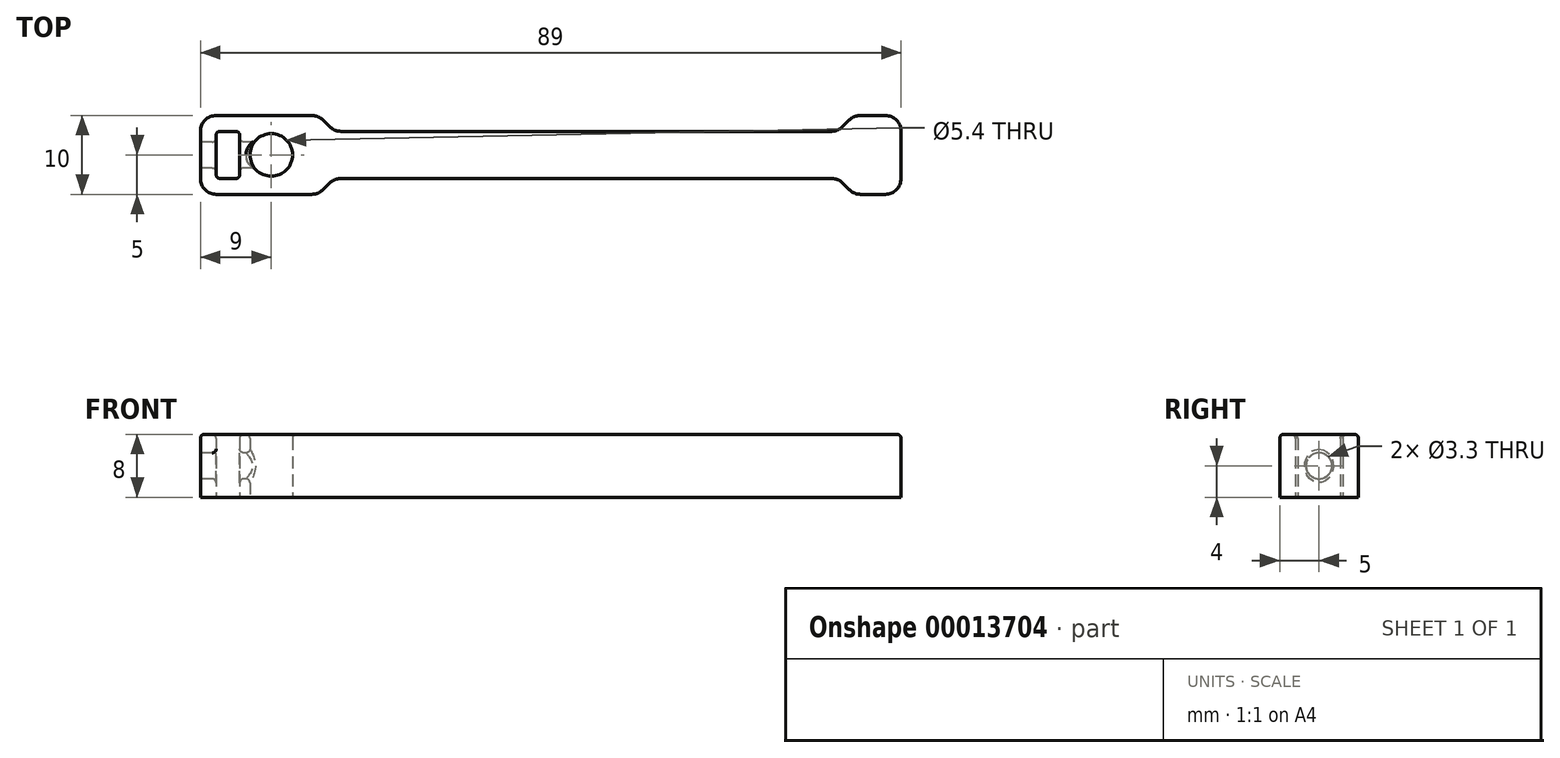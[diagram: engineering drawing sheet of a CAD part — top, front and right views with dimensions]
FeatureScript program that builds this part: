
annotation { "Feature Type Name" : "Feature", "Feature Type Description" : "" }
export const myFeature = defineFeature(function(context is Context, id is Id, definition is map)
    precondition{}
    {
        {
            var Q0;
            Q0=qCreatedBy(makeId("Top.planeOp"),FACE);
            var sketch = newSketch(context, id + "F0", { "sketchPlane" : qUnion([Q0])});
            skCircle(sketch, "E0", {"center": v(0, 0) * mm, "radius": 2.7 * mm});
            skLineSegment(sketch, "E1", {"start": v(0, 0) * mm, "end": v(80, 0) * mm, "construction": true});
            skLineSegment(sketch, "E2", {"start": v(-9, 5) * mm, "end": v(80, 5) * mm});
            skLineSegment(sketch, "E3", {"start": v(-9, -5) * mm, "end": v(80, -5) * mm});
            skLineSegment(sketch, "E4", {"start": v(80, -5) * mm, "end": v(80, 0) * mm});
            skLineSegment(sketch, "E5", {"start": v(80, 0) * mm, "end": v(80, 5) * mm});
            skLineSegment(sketch, "E6", {"start": v(-9, -5) * mm, "end": v(-9, 5) * mm});
            skLineSegment(sketch, "E7.rect.bottom", {"start": v(-4, 3) * mm, "end": v(-7, 3) * mm});
            skLineSegment(sketch, "E7.rect.top", {"start": v(-4, -3) * mm, "end": v(-7, -3) * mm});
            skLineSegment(sketch, "E7.rect.left", {"start": v(-4, 3) * mm, "end": v(-4, -3) * mm});
            skLineSegment(sketch, "E7.rect.right", {"start": v(-7, 3) * mm, "end": v(-7, -3) * mm});
            skPoint(sketch, "E7.rect.middle", {"position": v(-5.5, 0) * mm});
            skLineSegment(sketch, "E8", {"start": v(6, 5) * mm, "end": v(8, 3) * mm});
            skLineSegment(sketch, "E9", {"start": v(6, -5) * mm, "end": v(8, -3) * mm});
            skLineSegment(sketch, "E10", {"start": v(8, 3) * mm, "end": v(72, 3) * mm});
            skLineSegment(sketch, "E11", {"start": v(8, -3) * mm, "end": v(72, -3) * mm});
            skLineSegment(sketch, "E12", {"start": v(72, -3) * mm, "end": v(74, -5) * mm});
            skLineSegment(sketch, "E13", {"start": v(72, 3) * mm, "end": v(74, 5) * mm});
            skSolve(sketch);
        }
        {
            var Q0;
            Q0=makeQuery(id+"F0.imprint","IMPRINT",FACE,{"disambiguationData":[TD([[makeQuery(id+"F0.imprint","IMPRINT",EDGE,{"derivedFrom":sQuery(id+"F0.wireOp",EDGE,"E0")}),-1.0]])]});
            extrude(context, id + "F1", {"entities" : qUnion([Q0]), "depth" : 8 * mm});
        }
        {
            var Q0;
            Q0=makeQuery(id+"F1.opExtrude","SWEPT_FACE",FACE,{"disambiguationData":[OSD([sQuery(id+"F0.wireOp",EDGE,"E6")])]});
            var sketch = newSketch(context, id + "F2", { "sketchPlane" : qUnion([Q0])});
            skLineSegment(sketch, "E14", {"start": v(0, 8) * mm, "end": v(0, 0) * mm, "construction": true});
            skCircle(sketch, "E15", {"center": v(0, 4) * mm, "radius": 1.65 * mm});
            skSolve(sketch);
        }
        {
            var Q0;
            Q0=makeQuery(id+"F2.imprint","IMPRINT",FACE,{"disambiguationData":[TD([[makeQuery(id+"F2.imprint","IMPRINT",EDGE,{"derivedFrom":sQuery(id+"F2.wireOp",EDGE,"E15")}),1.0]])]});
            extrude(context, id + "F3", {"entities" : qUnion([Q0]), "operationType" : NewBodyOperationType.REMOVE, "oppositeDirection" : true, "depth" : 9 * mm});
        }
        {
            var Q0;
            Q0=makeQuery(id+"F1.opExtrude","SWEPT_EDGE",EDGE,{"disambiguationData":[OSD([sQuery(id+"F0.wireOp",EDGE,"E2"),sQuery(id+"F0.wireOp",EDGE,"E8")])]});
            var Q1;
            Q1=makeQuery(id+"F1.opExtrude","SWEPT_EDGE",EDGE,{"disambiguationData":[OSD([sQuery(id+"F0.wireOp",EDGE,"E8"),sQuery(id+"F0.wireOp",EDGE,"E10")])]});
            var Q2;
            Q2=makeQuery(id+"F1.opExtrude","SWEPT_EDGE",EDGE,{"disambiguationData":[OSD([sQuery(id+"F0.wireOp",EDGE,"E3"),sQuery(id+"F0.wireOp",EDGE,"E9")])]});
            var Q3;
            Q3=makeQuery(id+"F1.opExtrude","SWEPT_EDGE",EDGE,{"disambiguationData":[OSD([sQuery(id+"F0.wireOp",EDGE,"E9"),sQuery(id+"F0.wireOp",EDGE,"E11")])]});
            var Q4;
            Q4=makeQuery(id+"F1.opExtrude","SWEPT_EDGE",EDGE,{"disambiguationData":[OSD([sQuery(id+"F0.wireOp",EDGE,"E11"),sQuery(id+"F0.wireOp",EDGE,"E12")])]});
            var Q5;
            Q5=makeQuery(id+"F1.opExtrude","SWEPT_EDGE",EDGE,{"disambiguationData":[OSD([sQuery(id+"F0.wireOp",EDGE,"E3"),sQuery(id+"F0.wireOp",EDGE,"E12")])]});
            var Q6;
            Q6=makeQuery(id+"F1.opExtrude","SWEPT_EDGE",EDGE,{"disambiguationData":[OSD([sQuery(id+"F0.wireOp",EDGE,"E10"),sQuery(id+"F0.wireOp",EDGE,"E13")])]});
            var Q7;
            Q7=makeQuery(id+"F1.opExtrude","SWEPT_EDGE",EDGE,{"disambiguationData":[OSD([sQuery(id+"F0.wireOp",EDGE,"E2"),sQuery(id+"F0.wireOp",EDGE,"E13")])]});
            var Q8;
            Q8=makeQuery(id+"F1.opExtrude","SWEPT_EDGE",EDGE,{"disambiguationData":[OSD([sQuery(id+"F0.wireOp",EDGE,"E2"),sQuery(id+"F0.wireOp",EDGE,"E4")])]});
            var Q9;
            Q9=makeQuery(id+"F1.opExtrude","SWEPT_EDGE",EDGE,{"disambiguationData":[OSD([sQuery(id+"F0.wireOp",EDGE,"E3"),sQuery(id+"F0.wireOp",EDGE,"E4")])]});
            var Q10;
            Q10=makeQuery(id+"F1.opExtrude","SWEPT_EDGE",EDGE,{"disambiguationData":[OSD([sQuery(id+"F0.wireOp",EDGE,"E3"),sQuery(id+"F0.wireOp",EDGE,"E6")])]});
            var Q11;
            Q11=makeQuery(id+"F1.opExtrude","SWEPT_EDGE",EDGE,{"disambiguationData":[OSD([sQuery(id+"F0.wireOp",EDGE,"E2"),sQuery(id+"F0.wireOp",EDGE,"E6")])]});
            fillet(context, id + "F4", {"entities" : qUnion([Q0, Q1, Q2, Q3, Q4, Q5, Q6, Q7, Q8, Q9, Q10, Q11]), "radius" : 2 * mm, "tangentPropagation" : true, "allowEdgeOverflow" : false});
        }
        {
            var Q0;
            Q0=makeQuery(id+"F1.opExtrude","SWEPT_EDGE",EDGE,{"disambiguationData":[OSD([sQuery(id+"F0.wireOp",EDGE,"E7.rect.bottom"),sQuery(id+"F0.wireOp",EDGE,"E7.rect.left")])]});
            var Q1;
            Q1=makeQuery(id+"F1.opExtrude","SWEPT_EDGE",EDGE,{"disambiguationData":[OSD([sQuery(id+"F0.wireOp",EDGE,"E7.rect.bottom"),sQuery(id+"F0.wireOp",EDGE,"E7.rect.right")])]});
            var Q2;
            Q2=makeQuery(id+"F1.opExtrude","SWEPT_EDGE",EDGE,{"disambiguationData":[OSD([sQuery(id+"F0.wireOp",EDGE,"E7.rect.top"),sQuery(id+"F0.wireOp",EDGE,"E7.rect.right")])]});
            var Q3;
            Q3=makeQuery(id+"F1.opExtrude","SWEPT_EDGE",EDGE,{"disambiguationData":[OSD([sQuery(id+"F0.wireOp",EDGE,"E7.rect.top"),sQuery(id+"F0.wireOp",EDGE,"E7.rect.left")])]});
            fillet(context, id + "F5", {"entities" : qUnion([Q0, Q1, Q2, Q3]), "radius" : 0.5 * mm, "tangentPropagation" : true, "allowEdgeOverflow" : false});
        }
        {
            var Q0;
            Q0=makeQuery(id+"F1.opExtrude","CAP_EDGE",EDGE,{"disambiguationData":[OSD([sQuery(id+"F0.wireOp",EDGE,"E7.rect.bottom")])],"isStart":false});
            var Q1;
            Q1=makeQuery(id+"F1.opExtrude","CAP_EDGE",EDGE,{"disambiguationData":[OSD([sQuery(id+"F0.wireOp",EDGE,"E0")])],"isStart":false});
            var Q2;
            Q2=makeQuery(id+"F3.boolean.opBoolean","COPY",EDGE,{"derivedFrom":makeQuery(id+"F3.opExtrude","CAP_EDGE",EDGE,{"disambiguationData":[OSD([sQuery(id+"F2.wireOp",EDGE,"E15")])],"isStart":true})});
            var Q3;
            Q3=makeQuery(id+"F3.boolean.opBoolean","INTERSECT",EDGE,{"derivedFrom":[makeQuery(id+"F1.opExtrude","SWEPT_FACE",FACE,{"disambiguationData":[OSD([sQuery(id+"F0.wireOp",EDGE,"E7.rect.right")])]}),makeQuery(id+"F3.opExtrude","SWEPT_FACE",FACE,{"disambiguationData":[OSD([sQuery(id+"F2.wireOp",EDGE,"E15")])]})]});
            var Q4;
            Q4=makeQuery(id+"F3.boolean.opBoolean","INTERSECT",EDGE,{"derivedFrom":[makeQuery(id+"F1.opExtrude","SWEPT_FACE",FACE,{"disambiguationData":[OSD([sQuery(id+"F0.wireOp",EDGE,"E7.rect.left")])]}),makeQuery(id+"F3.opExtrude","SWEPT_FACE",FACE,{"disambiguationData":[OSD([sQuery(id+"F2.wireOp",EDGE,"E15")])]})]});
            var Q5;
            Q5=makeQuery(id+"F3.boolean.opBoolean","INTERSECT",EDGE,{"derivedFrom":[makeQuery(id+"F1.opExtrude","SWEPT_FACE",FACE,{"disambiguationData":[OSD([sQuery(id+"F0.wireOp",EDGE,"E0")])]}),makeQuery(id+"F3.opExtrude","SWEPT_FACE",FACE,{"disambiguationData":[OSD([sQuery(id+"F2.wireOp",EDGE,"E15")])]})]});
            var Q6;
            {var subQ0=sQuery(id+"F0.wireOp",EDGE,"E3");Q6=makeQuery(id+"F1.opExtrude","CAP_EDGE",EDGE,{"disambiguationData":[OSD([subQ0]),TDD([makeQuery(id+"F0.imprint","IMPRINT",EDGE,{"disambiguationData":[TD([[makeQuery(id+"F0.imprint","INTERSECT",VERTEX,{"derivedFrom":[subQ0,sQuery(id+"F0.wireOp",EDGE,"E6")]}),-1.0]])],"derivedFrom":subQ0})])],"isStart":false});}
            fillet(context, id + "F6", {"entities" : qUnion([Q0, Q1, Q2, Q3, Q4, Q5, Q6]), "radius" : 0.5 * mm, "tangentPropagation" : true, "allowEdgeOverflow" : false});
        }
    });
